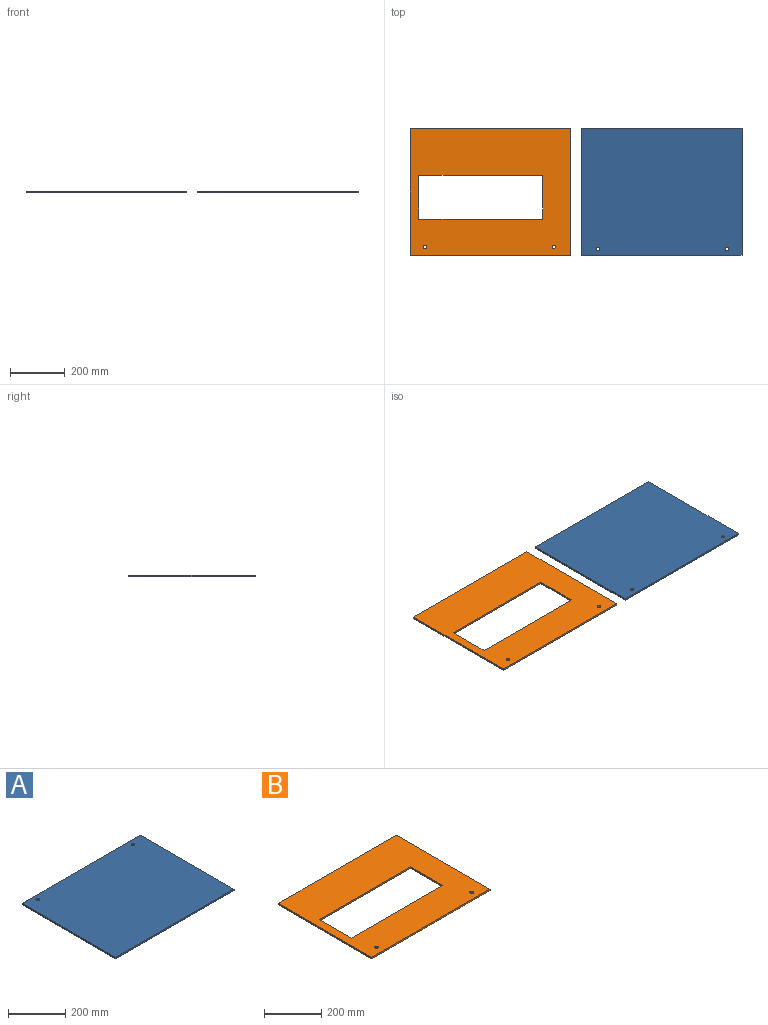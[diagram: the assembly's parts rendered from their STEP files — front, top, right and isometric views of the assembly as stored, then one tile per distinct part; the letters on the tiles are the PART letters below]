
ASSEMBLY  parts=2 mates=1
PART A: 8 faces, bbox 584.2x463.6x6.4 mm
  f0: plane 584.2x6.35mm, normal (0,-1,0), area 3709.7mm2, adj f1,f3,f4,f5
  f1: plane 463.55x6.35mm, normal (1,0,0), area 2943.5mm2, adj f0,f2,f4,f5
  f2: plane 584.2x6.35mm, normal (0,1,0), area 3709.7mm2, adj f1,f3,f4,f5
  f3: plane 463.55x6.35mm, normal (-1,0,0), area 2943.5mm2, adj f0,f2,f4,f5
  f4: plane 584.2x463.55mm, normal (0,0,1), area 270552.6mm2, adj f0,f1,f2,f3,f6,f7
  f5: plane 584.2x463.55mm, normal (0,0,-1), area 270552.6mm2, adj f0,f1,f2,f3,f6,f7
  f6: cylinder r=6.35mm len=12.7mm, axis (0,0,1), area 253.4mm2, adj f4,f5
  f7: cylinder r=6.35mm len=12.7mm, axis (0,0,1), area 253.4mm2, adj f4,f5
PART B: 12 faces, bbox 584.2x463.6x6.4 mm
  f0: plane 584.2x463.55mm, normal (0,0,1), area 198434mm2, adj f2,f3,f4,f5,f6,f7,f8,f9
  f1: plane 584.2x463.55mm, normal (0,0,-1), area 198434mm2, adj f2,f3,f4,f5,f6,f7,f8,f9
  f2: plane 584.2x6.35mm, normal (0,-1,0), area 3709.7mm2, adj f0,f1,f3,f5
  f3: plane 463.55x6.35mm, normal (1,0,0), area 2943.5mm2, adj f0,f1,f2,f4
  f4: plane 584.2x6.35mm, normal (0,1,0), area 3709.7mm2, adj f0,f1,f3,f5
  f5: plane 463.55x6.35mm, normal (-1,0,0), area 2943.5mm2, adj f0,f1,f2,f4
  f6: cylinder r=6.35mm len=12.7mm, axis (0,0,1), area 253.4mm2, adj f0,f1
  f7: cylinder r=6.35mm len=12.7mm, axis (0,0,1), area 253.4mm2, adj f0,f1
  f8: plane 159.51x6.35mm, normal (1,0,0), area 1012.9mm2, adj f0,f1,f9,f11
  f9: plane 452.12x6.35mm, normal (0,1,0), area 2871mm2, adj f0,f1,f8,f10
  f10: plane 159.51x6.35mm, normal (-1,0,0), area 1012.9mm2, adj f0,f1,f9,f11
  f11: plane 452.12x6.35mm, normal (0,-1,0), area 2871mm2, adj f0,f1,f8,f10
PLACE A rot(axis=(0,0,-1),180deg) t=(194.42,12.7,-6.12)mm
PLACE B t=(-433.34,12.64,-6.12)mm
MATE planar A.f5 <-> B.f1  axis (0,0,-1) through (194.42,12.9,-6.12)mm
